# Revit family: TOWELRAIL SMART 300
name_source: partatom
category: Mechanical Equipment
revit_build: Autodesk Revit 2018 (Build: 20180423_1000(x64)
units: mm (PartAtom-declared; Revit-internal decimal feet)

## family parameters
Always vertical = Yes
Classification = None
Cut with Voids When Loaded = No
OmniClass Number = 23.75.10.14.14.11
OmniClass Title = Storage Heaters
Part Type = Normal
Room Calculation Point = No
Round Connector Dimension = Use Diameter
Shared = No
Work Plane-Based = No

## types (1)
- TOWELRAIL SMART 300
    Art. No. = 428 000 300
    Breedte = 478 mm  [stored 1.56824 ft]
    Diepte = 25 mm  [stored 0.082021 ft]
    Hoogte = 933 mm  [stored 3.06102 ft]
    Manufacturer = Masterwatt B.V.
    Metaal = Metaal
    Model = Towel-smart-300
    URL = https://masterwatt.nl
    Wit = Laquer White
    Zwart rubber = Rubber

note: [stored X ft] marks values corroborated as IEEE doubles in the binary element streams (Revit-internal decimal feet)

## geometry (parser evidence)
native form markers: Sweep x7
no freeform markers — native parametric forms only
